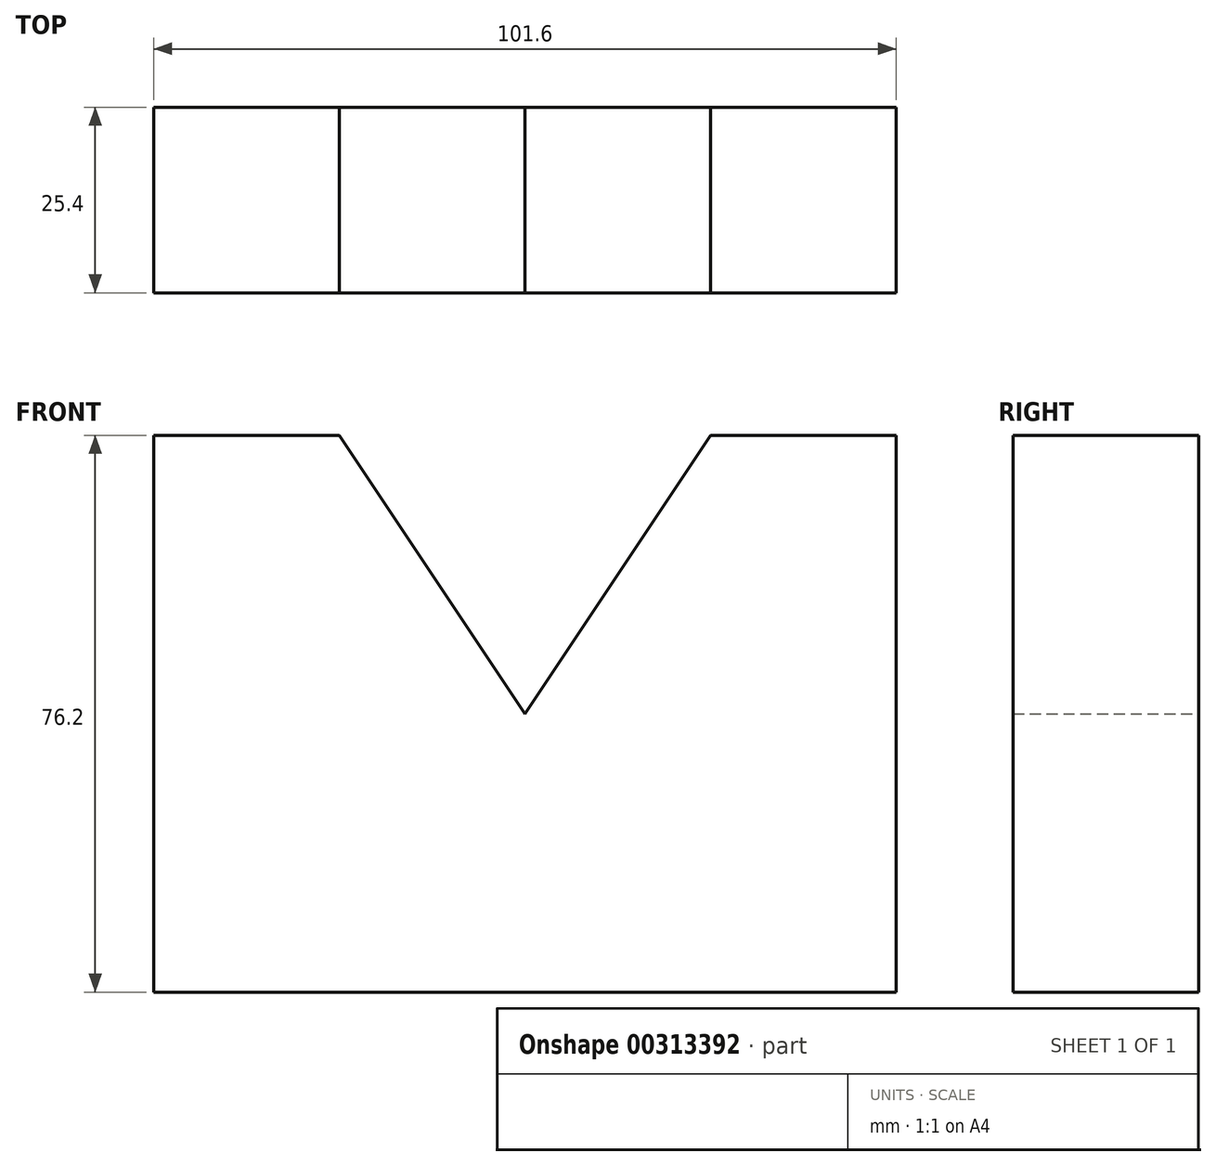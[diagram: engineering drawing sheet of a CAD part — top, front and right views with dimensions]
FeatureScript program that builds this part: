
annotation { "Feature Type Name" : "Feature", "Feature Type Description" : "" }
export const myFeature = defineFeature(function(context is Context, id is Id, definition is map)
    precondition{}
    {
        {
            var Q0;
            Q0=qCreatedBy(makeId("Front.planeOp"),FACE);
            var sketch = newSketch(context, id + "F0", { "sketchPlane" : qUnion([Q0])});
            skLineSegment(sketch, "E0", {"start": v(-50.95, -51.53) * mm, "end": v(50.65, -51.53) * mm});
            skLineSegment(sketch, "E1", {"start": v(-50.95, -51.53) * mm, "end": v(-50.95, 24.67) * mm});
            skLineSegment(sketch, "E2", {"start": v(50.65, -51.53) * mm, "end": v(50.65, 24.67) * mm});
            skLineSegment(sketch, "E3", {"start": v(-50.95, 24.67) * mm, "end": v(-25.55, 24.67) * mm});
            skLineSegment(sketch, "E4", {"start": v(50.65, 24.67) * mm, "end": v(25.25, 24.67) * mm});
            skPoint(sketch, "E5.startSnap0", {"position": v(-50.95, -13.43) * mm});
            skLineSegment(sketch, "E6", {"start": v(-0.15, -13.43) * mm, "end": v(25.25, 24.67) * mm});
            skPoint(sketch, "E6.startSnap0", {"position": v(-0.15, -51.53) * mm});
            skLineSegment(sketch, "E7", {"start": v(-25.55, 24.67) * mm, "end": v(-0.15, -13.43) * mm});
            skSolve(sketch);
        }
        {
            var Q0;
            Q0=makeQuery(id+"F0.imprint","IMPRINT",FACE,{"disambiguationData":[TD([[makeQuery(id+"F0.imprint","IMPRINT",EDGE,{"derivedFrom":sQuery(id+"F0.wireOp",EDGE,"E0")}),1.0]])]});
            extrude(context, id + "F1", {"entities" : qUnion([Q0]), "depth" : 25.4 * mm});
        }
    });
